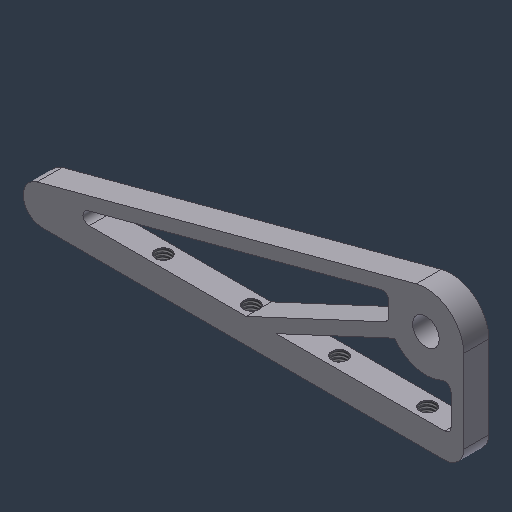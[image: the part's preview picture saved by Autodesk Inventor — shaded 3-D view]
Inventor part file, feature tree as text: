
AUTODESK INVENTOR PART (.ipt)
format: ipt  version: 2024.3 (Build 283343000, 343)  size: 178,176 bytes
history: native  units: mm (DEFAULTED — no unit token found)
features: sketch x3, hole x2, extrude x1, fillet x1, pattern_linear x1
ambient origin geometry x8: Origin, YZ Plane, XZ Plane, XY Plane, X Axis, Y Axis, Z Axis, Center Point
bodies: Solid1 (feature_tree)
feature tree (8):
  extrude  "Extrusion1"  Depth=9.525mm
  fillet  "Fillet1"  Radius=4.7625mm
  hole  "Hole2"  [1 undecoded]
  hole  "Hole3"  [1 undecoded]
  pattern_linear  "Rectangular Pattern2"  Spacing1=101.6mm  [1 undecoded]
  sketch  "Sketch2"  dims[d0=38.1mm d2=9.525mm d3=4.7625mm]
  sketch  "Sketch4"  dims[d4=9.525mm d7=3.175mm]
  sketch  "Sketch5"  dims[d8=6.35mm d9=0.0mm d20=1.5875mm d21=6.7564mm d22=9.652mm d23=12.8778mm d24=1.9558mm d25=14.3117mm d26=25.4mm d27=20.594885mm d28=101.6mm d29=3.175mm d31=3.175mm d32=4.363323mm d33=6.35mm d35=12.272716mm d36=3.175489mm d37=3.9624mm d38=9.652mm d39=9.525mm d40=6.35mm d41=14.3117mm d42=13.6144mm d43=20.594885mm d44=50.0mm d46=22.225mm d5=0.872665mm]
note: 3 required parameter values undecoded (feature->parameter linkage not recoverable at this tier; creation-order binding heuristic only, values carry confidence <= 0.55)
